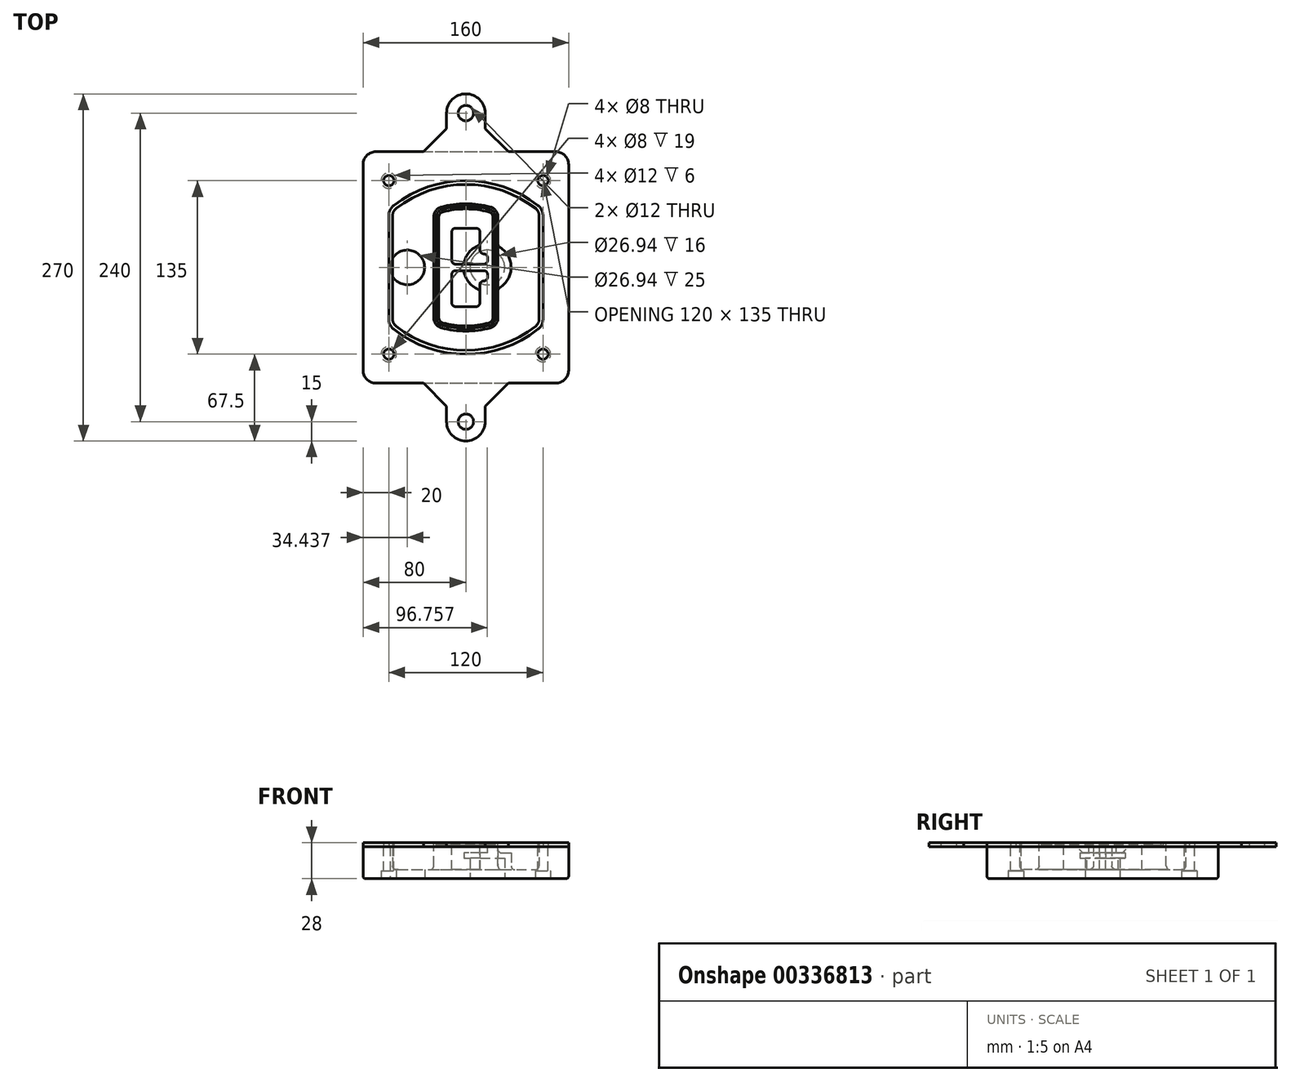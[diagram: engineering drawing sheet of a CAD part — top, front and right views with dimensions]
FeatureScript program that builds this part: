
annotation { "Feature Type Name" : "Feature", "Feature Type Description" : "" }
export const myFeature = defineFeature(function(context is Context, id is Id, definition is map)
    precondition{}
    {
        {
            var Q0;
            Q0=qCreatedBy(makeId("Top.planeOp"),FACE);
            var sketch = newSketch(context, id + "F0", { "sketchPlane" : qUnion([Q0])});
            skPoint(sketch, "E0.rect.middle", {"position": v(0, 0) * mm});
            skLineSegment(sketch, "E1.bottom", {"start": v(-70, -90) * mm, "end": v(70, -90) * mm});
            skLineSegment(sketch, "E1.top", {"start": v(-70, 90) * mm, "end": v(70, 90) * mm});
            skLineSegment(sketch, "E1.left", {"start": v(-80, -80) * mm, "end": v(-80, 80) * mm});
            skLineSegment(sketch, "E1.right", {"start": v(80, -80) * mm, "end": v(80, 80) * mm});
            skLineSegment(sketch, "E2", {"start": v(-80, 90) * mm, "end": v(80, -90) * mm, "construction": true});
            skLineSegment(sketch, "E3", {"start": v(80, 90) * mm, "end": v(-80, -90) * mm, "construction": true});
            skCircle(sketch, "E4", {"center": v(-60, 67.5) * mm, "radius": 4 * mm});
            skCircle(sketch, "E5", {"center": v(60, 67.5) * mm, "radius": 4 * mm});
            skCircle(sketch, "E6", {"center": v(60, -67.5) * mm, "radius": 4 * mm});
            skCircle(sketch, "E7", {"center": v(-60, -67.5) * mm, "radius": 4 * mm});
            skLineSegment(sketch, "E8", {"start": v(-60, 67.5) * mm, "end": v(60, 67.5) * mm, "construction": true});
            skLineSegment(sketch, "E9", {"start": v(60, 67.5) * mm, "end": v(60, -67.5) * mm, "construction": true});
            skLineSegment(sketch, "E10", {"start": v(60, -67.5) * mm, "end": v(-60, -67.5) * mm, "construction": true});
            skLineSegment(sketch, "E11", {"start": v(-60, -67.5) * mm, "end": v(-60, 67.5) * mm, "construction": true});
            skLineSegment(sketch, "E12", {"start": v(-60, 40.3) * mm, "end": v(-60, -40.3) * mm});
            skLineSegment(sketch, "E13", {"start": v(60, 40.3) * mm, "end": v(60, -40.3) * mm});
            skArc(sketch, "E14", {"start": v(56.15, 48.18) * mm, "mid": v(0, 67.5) * mm, "end": v(-56.15, 48.18) * mm});
            skArc(sketch, "E15", {"start": v(-56.15, -48.18) * mm, "mid": v(0, -67.5) * mm, "end": v(56.15, -48.18) * mm});
            skLineSegment(sketch, "E16", {"start": v(-60, 0) * mm, "end": v(60, 0) * mm, "construction": true});
            skPoint(sketch, "E17.visualSharp", {"position": v(-60, -45) * mm});
            skArc(sketch, "E17.filletArc", {"start": v(-60, -40.3) * mm, "mid": v(-58.99, -44.68) * mm, "end": v(-56.15, -48.18) * mm});
            skPoint(sketch, "E18.visualSharp", {"position": v(-60, 45) * mm});
            skArc(sketch, "E18.filletArc", {"start": v(-56.15, 48.18) * mm, "mid": v(-58.99, 44.68) * mm, "end": v(-60, 40.3) * mm});
            skPoint(sketch, "E19.visualSharp", {"position": v(60, 45) * mm});
            skArc(sketch, "E19.filletArc", {"start": v(60, 40.3) * mm, "mid": v(58.99, 44.68) * mm, "end": v(56.15, 48.18) * mm});
            skPoint(sketch, "E20.visualSharp", {"position": v(60, -45) * mm});
            skArc(sketch, "E20.filletArc", {"start": v(56.15, -48.18) * mm, "mid": v(58.99, -44.68) * mm, "end": v(60, -40.3) * mm});
            skPoint(sketch, "E21.visualSharp", {"position": v(-80, 90) * mm});
            skArc(sketch, "E21.filletArc", {"start": v(-70, 90) * mm, "mid": v(-77.07, 87.07) * mm, "end": v(-80, 80) * mm});
            skPoint(sketch, "E22.visualSharp", {"position": v(80, 90) * mm});
            skArc(sketch, "E22.filletArc", {"start": v(80, 80) * mm, "mid": v(77.07, 87.07) * mm, "end": v(70, 90) * mm});
            skPoint(sketch, "E23.visualSharp", {"position": v(80, -90) * mm});
            skArc(sketch, "E23.filletArc", {"start": v(70, -90) * mm, "mid": v(77.07, -87.07) * mm, "end": v(80, -80) * mm});
            skPoint(sketch, "E24.visualSharp", {"position": v(-80, -90) * mm});
            skArc(sketch, "E24.filletArc", {"start": v(-80, -80) * mm, "mid": v(-77.07, -87.07) * mm, "end": v(-70, -90) * mm});
            skArc(sketch, "E25.0", {"start": v(57, 40.3) * mm, "mid": v(56.3, 43.36) * mm, "end": v(54.3, 45.81) * mm});
            skLineSegment(sketch, "E25.1", {"start": v(57, 40.3) * mm, "end": v(57, -40.3) * mm});
            skArc(sketch, "E25.2", {"start": v(54.3, -45.81) * mm, "mid": v(56.3, -43.36) * mm, "end": v(57, -40.3) * mm});
            skArc(sketch, "E25.3", {"start": v(-54.3, -45.81) * mm, "mid": v(0, -64.5) * mm, "end": v(54.3, -45.81) * mm});
            skArc(sketch, "E25.4", {"start": v(-57, -40.3) * mm, "mid": v(-56.3, -43.36) * mm, "end": v(-54.3, -45.81) * mm});
            skArc(sketch, "E25.5", {"start": v(54.3, 45.81) * mm, "mid": v(0, 64.5) * mm, "end": v(-54.3, 45.81) * mm});
            skLineSegment(sketch, "E25.6", {"start": v(-57, 40.3) * mm, "end": v(-57, -40.3) * mm});
            skArc(sketch, "E25.7", {"start": v(-54.3, 45.81) * mm, "mid": v(-56.3, 43.36) * mm, "end": v(-57, 40.3) * mm});
            skArc(sketch, "E26.0", {"start": v(-58.62, 51.33) * mm, "mid": v(-62.58, 46.43) * mm, "end": v(-64, 40.3) * mm});
            skArc(sketch, "E26.1", {"start": v(58.62, 51.33) * mm, "mid": v(0, 71.5) * mm, "end": v(-58.62, 51.33) * mm});
            skArc(sketch, "E26.2", {"start": v(64, 40.3) * mm, "mid": v(62.58, 46.43) * mm, "end": v(58.62, 51.33) * mm});
            skLineSegment(sketch, "E26.3", {"start": v(64, 40.3) * mm, "end": v(64, -40.3) * mm});
            skArc(sketch, "E26.4", {"start": v(58.62, -51.33) * mm, "mid": v(62.58, -46.43) * mm, "end": v(64, -40.3) * mm});
            skLineSegment(sketch, "E26.5", {"start": v(-64, 40.3) * mm, "end": v(-64, -40.3) * mm});
            skArc(sketch, "E26.6", {"start": v(-58.62, -51.33) * mm, "mid": v(0, -71.5) * mm, "end": v(58.62, -51.33) * mm});
            skArc(sketch, "E26.7", {"start": v(-64, -40.3) * mm, "mid": v(-62.58, -46.43) * mm, "end": v(-58.62, -51.33) * mm});
            skPoint(sketch, "E27.endSnap0", {"position": v(0, 90) * mm});
            skSolve(sketch);
        }
        {
            var Q0;
            Q0=makeQuery(id+"F0.imprint","IMPRINT",FACE,{"disambiguationData":[TD([[makeQuery(id+"F0.imprint","IMPRINT",EDGE,{"derivedFrom":sQuery(id+"F0.wireOp",EDGE,"E1.bottom")}),1.0]])]});
            var Q1;
            Q1=makeQuery(id+"F0.imprint","IMPRINT",FACE,{"disambiguationData":[TD([[makeQuery(id+"F0.imprint","IMPRINT",EDGE,{"derivedFrom":sQuery(id+"F0.wireOp",EDGE,"E12")}),1.0]])]});
            var Q2;
            Q2=makeQuery(id+"F0.imprint","IMPRINT",FACE,{"disambiguationData":[TD([[makeQuery(id+"F0.imprint","IMPRINT",EDGE,{"derivedFrom":sQuery(id+"F0.wireOp",EDGE,"E25.0")}),1.0]])]});
            var Q3;
            Q3=makeQuery(id+"F0.imprint","IMPRINT",FACE,{"disambiguationData":[TD([[makeQuery(id+"F0.imprint","IMPRINT",EDGE,{"derivedFrom":sQuery(id+"F0.wireOp",EDGE,"E12")}),-1.0]])]});
            extrude(context, id + "F1", {"entities" : qUnion([Q0, Q1, Q2, Q3]), "oppositeDirection" : true, "depth" : 25 * mm});
        }
        {
            var Q0;
            Q0=makeQuery(id+"F0.imprint","IMPRINT",FACE,{"disambiguationData":[TD([[makeQuery(id+"F0.imprint","IMPRINT",EDGE,{"derivedFrom":sQuery(id+"F0.wireOp",EDGE,"E12")}),1.0]])]});
            extrude(context, id + "F2", {"entities" : qUnion([Q0]), "operationType" : NewBodyOperationType.ADD, "depth" : 3 * mm});
        }
        {
            var Q0;
            Q0=makeQuery(id+"F0.imprint","IMPRINT",FACE,{"disambiguationData":[TD([[makeQuery(id+"F0.imprint","IMPRINT",EDGE,{"derivedFrom":sQuery(id+"F0.wireOp",EDGE,"E25.0")}),1.0]])]});
            extrude(context, id + "F3", {"entities" : qUnion([Q0]), "operationType" : NewBodyOperationType.REMOVE, "oppositeDirection" : true, "depth" : 18 * mm});
        }
        {
            var Q0;
            Q0=makeQuery(id+"F2.opExtrude","CAP_FACE",FACE,{"disambiguationData":[OSD([sQuery(id+"F0.wireOp",EDGE,"E12"),sQuery(id+"F0.wireOp",EDGE,"E13"),sQuery(id+"F0.wireOp",EDGE,"E14"),sQuery(id+"F0.wireOp",EDGE,"E15"),sQuery(id+"F0.wireOp",EDGE,"E17.filletArc"),sQuery(id+"F0.wireOp",EDGE,"E18.filletArc"),sQuery(id+"F0.wireOp",EDGE,"E19.filletArc"),sQuery(id+"F0.wireOp",EDGE,"E20.filletArc"),sQuery(id+"F0.wireOp",EDGE,"E25.0"),sQuery(id+"F0.wireOp",EDGE,"E25.1"),sQuery(id+"F0.wireOp",EDGE,"E25.2"),sQuery(id+"F0.wireOp",EDGE,"E25.3"),sQuery(id+"F0.wireOp",EDGE,"E25.4"),sQuery(id+"F0.wireOp",EDGE,"E25.5"),sQuery(id+"F0.wireOp",EDGE,"E25.6"),sQuery(id+"F0.wireOp",EDGE,"E25.7")])],"isStart":false});
            var sketch = newSketch(context, id + "F4", { "sketchPlane" : qUnion([Q0])});
            skArc(sketch, "E28.0", {"start": v(-19.08, -46.97) * mm, "mid": v(0, -49.5) * mm, "end": v(19.08, -46.97) * mm});
            skArc(sketch, "E29.0", {"start": v(19.08, 46.97) * mm, "mid": v(0, 49.5) * mm, "end": v(-19.08, 46.97) * mm});
            skLineSegment(sketch, "E30", {"start": v(-25, 39.25) * mm, "end": v(-25, -39.25) * mm});
            skLineSegment(sketch, "E31", {"start": v(25, 39.25) * mm, "end": v(25, -39.25) * mm});
            skLineSegment(sketch, "E32", {"start": v(-25, 45.1) * mm, "end": v(25, 45.1) * mm, "construction": true});
            skLineSegment(sketch, "E33", {"start": v(-25, -45.1) * mm, "end": v(25, -45.1) * mm, "construction": true});
            skPoint(sketch, "E34.visualSharp", {"position": v(-25, 45.1) * mm});
            skArc(sketch, "E34.filletArc", {"start": v(-19.08, 46.97) * mm, "mid": v(-23.35, 44.11) * mm, "end": v(-25, 39.25) * mm});
            skPoint(sketch, "E35.visualSharp", {"position": v(25, 45.1) * mm});
            skArc(sketch, "E35.filletArc", {"start": v(25, 39.25) * mm, "mid": v(23.35, 44.11) * mm, "end": v(19.08, 46.97) * mm});
            skPoint(sketch, "E36.visualSharp", {"position": v(25, -45.1) * mm});
            skArc(sketch, "E36.filletArc", {"start": v(19.08, -46.97) * mm, "mid": v(23.35, -44.11) * mm, "end": v(25, -39.25) * mm});
            skPoint(sketch, "E37.visualSharp", {"position": v(-25, -45.1) * mm});
            skArc(sketch, "E37.filletArc", {"start": v(-25, -39.25) * mm, "mid": v(-23.35, -44.11) * mm, "end": v(-19.08, -46.97) * mm});
            skArc(sketch, "E38.0", {"start": v(54.3, 45.81) * mm, "mid": v(0, 64.5) * mm, "end": v(-54.3, 45.81) * mm});
            skArc(sketch, "E38.1", {"start": v(-54.3, 45.81) * mm, "mid": v(-56.3, 43.36) * mm, "end": v(-57, 40.3) * mm});
            skLineSegment(sketch, "E38.2", {"start": v(-57, 40.3) * mm, "end": v(-57, -40.3) * mm});
            skArc(sketch, "E38.3", {"start": v(-57, -40.3) * mm, "mid": v(-56.3, -43.36) * mm, "end": v(-54.3, -45.81) * mm});
            skArc(sketch, "E38.4", {"start": v(-54.3, -45.81) * mm, "mid": v(0, -64.5) * mm, "end": v(54.3, -45.81) * mm});
            skArc(sketch, "E38.5", {"start": v(54.3, -45.81) * mm, "mid": v(56.3, -43.36) * mm, "end": v(57, -40.3) * mm});
            skLineSegment(sketch, "E38.6", {"start": v(57, 40.3) * mm, "end": v(57, -40.3) * mm});
            skArc(sketch, "E38.7", {"start": v(57, 40.3) * mm, "mid": v(56.3, 43.36) * mm, "end": v(54.3, 45.81) * mm});
            skLineSegment(sketch, "E39.0", {"start": v(23, 39.25) * mm, "end": v(23, -39.25) * mm});
            skArc(sketch, "E39.1", {"start": v(18.56, -45.04) * mm, "mid": v(21.76, -42.9) * mm, "end": v(23, -39.25) * mm});
            skArc(sketch, "E39.2", {"start": v(-18.56, -45.04) * mm, "mid": v(0, -47.5) * mm, "end": v(18.56, -45.04) * mm});
            skArc(sketch, "E39.3", {"start": v(-23, -39.25) * mm, "mid": v(-21.76, -42.9) * mm, "end": v(-18.56, -45.04) * mm});
            skLineSegment(sketch, "E39.4", {"start": v(-23, 39.25) * mm, "end": v(-23, -39.25) * mm});
            skArc(sketch, "E39.5", {"start": v(23, 39.25) * mm, "mid": v(21.76, 42.9) * mm, "end": v(18.56, 45.04) * mm});
            skArc(sketch, "E39.6", {"start": v(-18.56, 45.04) * mm, "mid": v(-21.76, 42.9) * mm, "end": v(-23, 39.25) * mm});
            skArc(sketch, "E39.7", {"start": v(18.56, 45.04) * mm, "mid": v(0, 47.5) * mm, "end": v(-18.56, 45.04) * mm});
            skArc(sketch, "E40.0", {"start": v(21, 39.25) * mm, "mid": v(20.18, 41.68) * mm, "end": v(18.04, 43.1) * mm});
            skLineSegment(sketch, "E40.1", {"start": v(21, 39.25) * mm, "end": v(21, -39.25) * mm});
            skArc(sketch, "E40.2", {"start": v(18.04, -43.1) * mm, "mid": v(20.18, -41.68) * mm, "end": v(21, -39.25) * mm});
            skArc(sketch, "E40.3", {"start": v(-18.04, -43.1) * mm, "mid": v(0, -45.5) * mm, "end": v(18.04, -43.1) * mm});
            skArc(sketch, "E40.4", {"start": v(-21, -39.25) * mm, "mid": v(-20.18, -41.68) * mm, "end": v(-18.04, -43.1) * mm});
            skArc(sketch, "E40.5", {"start": v(18.04, 43.1) * mm, "mid": v(0, 45.5) * mm, "end": v(-18.04, 43.1) * mm});
            skLineSegment(sketch, "E40.6", {"start": v(-21, 39.25) * mm, "end": v(-21, -39.25) * mm});
            skArc(sketch, "E40.7", {"start": v(-18.04, 43.1) * mm, "mid": v(-20.18, 41.68) * mm, "end": v(-21, 39.25) * mm});
            skLineSegment(sketch, "E41", {"start": v(-25, 0) * mm, "end": v(25, 0) * mm, "construction": true});
            skLineSegment(sketch, "E42", {"start": v(-11, 5.5) * mm, "end": v(-11, 27.5) * mm});
            skLineSegment(sketch, "E43", {"start": v(-8, 30.5) * mm, "end": v(8, 30.5) * mm});
            skLineSegment(sketch, "E44", {"start": v(11, 27.5) * mm, "end": v(11, 13.5) * mm});
            skLineSegment(sketch, "E45", {"start": v(14, 10.5) * mm, "end": v(14, 10.5) * mm});
            skLineSegment(sketch, "E46", {"start": v(17, 7.5) * mm, "end": v(17, 5.5) * mm});
            skLineSegment(sketch, "E47", {"start": v(14, 2.5) * mm, "end": v(-8, 2.5) * mm});
            skPoint(sketch, "E48.visualSharp", {"position": v(-11, 30.5) * mm});
            skArc(sketch, "E48.filletArc", {"start": v(-8, 30.5) * mm, "mid": v(-10.12, 29.62) * mm, "end": v(-11, 27.5) * mm});
            skPoint(sketch, "E49.visualSharp", {"position": v(11, 30.5) * mm});
            skArc(sketch, "E49.filletArc", {"start": v(11, 27.5) * mm, "mid": v(10.12, 29.62) * mm, "end": v(8, 30.5) * mm});
            skPoint(sketch, "E50.visualSharp", {"position": v(11, 10.5) * mm});
            skArc(sketch, "E50.filletArc", {"start": v(11, 13.5) * mm, "mid": v(11.88, 11.38) * mm, "end": v(14, 10.5) * mm});
            skPoint(sketch, "E51.visualSharp", {"position": v(17, 10.5) * mm});
            skArc(sketch, "E51.filletArc", {"start": v(17, 7.5) * mm, "mid": v(16.12, 9.62) * mm, "end": v(14, 10.5) * mm});
            skPoint(sketch, "E52.visualSharp", {"position": v(17, 2.5) * mm});
            skArc(sketch, "E52.filletArc", {"start": v(14, 2.5) * mm, "mid": v(16.12, 3.38) * mm, "end": v(17, 5.5) * mm});
            skPoint(sketch, "E53.visualSharp", {"position": v(-11, 2.5) * mm});
            skArc(sketch, "E53.filletArc", {"start": v(-11, 5.5) * mm, "mid": v(-10.12, 3.38) * mm, "end": v(-8, 2.5) * mm});
            skLineSegment(sketch, "E54.0.MirrorCS", {"start": v(14, -2.5) * mm, "end": v(-8, -2.5) * mm});
            skArc(sketch, "E55.0.MirrorCS", {"start": v(-11, -5.5) * mm, "mid": v(-10.12, -3.38) * mm, "end": v(-8, -2.5) * mm});
            skLineSegment(sketch, "E56.0.MirrorCS", {"start": v(-11, -5.5) * mm, "end": v(-11, -27.5) * mm});
            skArc(sketch, "E57.0.MirrorCS", {"start": v(-8, -30.5) * mm, "mid": v(-10.12, -29.62) * mm, "end": v(-11, -27.5) * mm});
            skLineSegment(sketch, "E58.0.MirrorCS", {"start": v(-8, -30.5) * mm, "end": v(8, -30.5) * mm});
            skArc(sketch, "E59.0.MirrorCS", {"start": v(11, -27.5) * mm, "mid": v(10.12, -29.62) * mm, "end": v(8, -30.5) * mm});
            skLineSegment(sketch, "E60.0.MirrorCS", {"start": v(11, -27.5) * mm, "end": v(11, -13.5) * mm});
            skArc(sketch, "E61.0.MirrorCS", {"start": v(11, -13.5) * mm, "mid": v(11.88, -11.38) * mm, "end": v(14, -10.5) * mm});
            skArc(sketch, "E62.0.MirrorCS", {"start": v(17, -7.5) * mm, "mid": v(16.12, -9.62) * mm, "end": v(14, -10.5) * mm});
            skLineSegment(sketch, "E63.0.MirrorCS", {"start": v(17, -7.5) * mm, "end": v(17, -5.5) * mm});
            skArc(sketch, "E64.0.MirrorCS", {"start": v(14, -2.5) * mm, "mid": v(16.12, -3.38) * mm, "end": v(17, -5.5) * mm});
            skSolve(sketch);
        }
        {
            var Q0;
            Q0=makeQuery(id+"F4.imprint","IMPRINT",FACE,{"disambiguationData":[TD([[makeQuery(id+"F4.imprint","IMPRINT",EDGE,{"derivedFrom":sQuery(id+"F4.wireOp",EDGE,"E28.0")}),1.0]])]});
            var Q1;
            Q1=makeQuery(id+"F4.imprint","IMPRINT",FACE,{"disambiguationData":[TD([[makeQuery(id+"F4.imprint","IMPRINT",EDGE,{"derivedFrom":sQuery(id+"F4.wireOp",EDGE,"E39.0")}),-1.0]])]});
            var Q2;
            Q2=makeQuery(id+"F4.imprint","IMPRINT",FACE,{"disambiguationData":[TD([[makeQuery(id+"F4.imprint","IMPRINT",EDGE,{"derivedFrom":sQuery(id+"F4.wireOp",EDGE,"E40.0")}),1.0]])]});
            extrude(context, id + "F5", {"entities" : qUnion([Q0, Q1, Q2]), "operationType" : NewBodyOperationType.ADD, "endBound" : BoundingType.UP_TO_NEXT, "oppositeDirection" : true, "depth" : 25 * mm});
        }
        {
            var Q0;
            Q0=makeQuery(id+"F4.imprint","IMPRINT",FACE,{"disambiguationData":[TD([[makeQuery(id+"F4.imprint","IMPRINT",EDGE,{"derivedFrom":sQuery(id+"F4.wireOp",EDGE,"E39.0")}),-1.0]])]});
            extrude(context, id + "F6", {"entities" : qUnion([Q0]), "operationType" : NewBodyOperationType.REMOVE, "oppositeDirection" : true, "depth" : 2 * mm});
        }
        {
            var Q0;
            Q0=makeQuery(id+"F1.opExtrude","CAP_FACE",FACE,{"disambiguationData":[OSD([sQuery(id+"F0.wireOp",EDGE,"E1.bottom"),sQuery(id+"F0.wireOp",EDGE,"E1.top"),sQuery(id+"F0.wireOp",EDGE,"E1.left"),sQuery(id+"F0.wireOp",EDGE,"E1.right"),sQuery(id+"F0.wireOp",EDGE,"E4"),sQuery(id+"F0.wireOp",EDGE,"E5"),sQuery(id+"F0.wireOp",EDGE,"E6"),sQuery(id+"F0.wireOp",EDGE,"E7"),sQuery(id+"F0.wireOp",EDGE,"E21.filletArc"),sQuery(id+"F0.wireOp",EDGE,"E22.filletArc"),sQuery(id+"F0.wireOp",EDGE,"E23.filletArc"),sQuery(id+"F0.wireOp",EDGE,"E24.filletArc")])],"isStart":false});
            var sketch = newSketch(context, id + "F7", { "sketchPlane" : qUnion([Q0])});
            skCircle(sketch, "E65", {"center": v(16.76, 0) * mm, "radius": 13.47 * mm});
            skCircle(sketch, "E66", {"center": v(-45.56, 0) * mm, "radius": 13.47 * mm});
            skLineSegment(sketch, "E67", {"start": v(80, 0) * mm, "end": v(-80, 0) * mm});
            skCircle(sketch, "E68", {"center": v(16.76, 0) * mm, "radius": 18.47 * mm});
            skCircle(sketch, "E69", {"center": v(60, -67.5) * mm, "radius": 6 * mm});
            skCircle(sketch, "E70", {"center": v(-60, -67.5) * mm, "radius": 6 * mm});
            skCircle(sketch, "E71", {"center": v(-60, 67.5) * mm, "radius": 6 * mm});
            skCircle(sketch, "E72", {"center": v(60, 67.5) * mm, "radius": 6 * mm});
            skSolve(sketch);
        }
        {
            var Q0;
            {var subQ1=sQuery(id+"F7.wireOp",EDGE,"E67");var subQ4=sQuery(id+"F7.wireOp",EDGE,"E65");var subQ6=makeQuery(id+"F7.imprint","INTERSECT",VERTEX,{"disambiguationData":[OD(0.0)],"derivedFrom":[subQ4,subQ1]});Q0=makeQuery(id+"F7.imprint","IMPRINT",FACE,{"disambiguationData":[TD([[makeQuery(id+"F7.imprint","IMPRINT",EDGE,{"disambiguationData":[TD([[subQ6,-1.0]])],"derivedFrom":subQ4}),-1.0]])]});}
            var Q1;
            {var subQ0=sQuery(id+"F7.wireOp",EDGE,"E67");var subQ1=sQuery(id+"F7.wireOp",EDGE,"E65");var subQ3=makeQuery(id+"F7.imprint","INTERSECT",VERTEX,{"disambiguationData":[OD(0.0)],"derivedFrom":[subQ1,subQ0]});Q1=makeQuery(id+"F7.imprint","IMPRINT",FACE,{"disambiguationData":[TD([[makeQuery(id+"F7.imprint","IMPRINT",EDGE,{"disambiguationData":[TD([[subQ3,-1.0]])],"derivedFrom":subQ1}),1.0]])]});}
            var Q2;
            {var subQ0=sQuery(id+"F7.wireOp",EDGE,"E67");var subQ1=sQuery(id+"F7.wireOp",EDGE,"E65");var subQ3=makeQuery(id+"F7.imprint","INTERSECT",VERTEX,{"disambiguationData":[OD(0.0)],"derivedFrom":[subQ1,subQ0]});Q2=makeQuery(id+"F7.imprint","IMPRINT",FACE,{"disambiguationData":[TD([[makeQuery(id+"F7.imprint","IMPRINT",EDGE,{"disambiguationData":[TD([[subQ3,1.0]])],"derivedFrom":subQ1}),1.0]])]});}
            var Q3;
            {var subQ1=sQuery(id+"F7.wireOp",EDGE,"E67");var subQ4=sQuery(id+"F7.wireOp",EDGE,"E65");var subQ6=makeQuery(id+"F7.imprint","INTERSECT",VERTEX,{"disambiguationData":[OD(0.0)],"derivedFrom":[subQ4,subQ1]});Q3=makeQuery(id+"F7.imprint","IMPRINT",FACE,{"disambiguationData":[TD([[makeQuery(id+"F7.imprint","IMPRINT",EDGE,{"disambiguationData":[TD([[subQ6,1.0]])],"derivedFrom":subQ4}),-1.0]])]});}
            extrude(context, id + "F8", {"entities" : qUnion([Q0, Q1, Q2, Q3]), "operationType" : NewBodyOperationType.ADD, "oppositeDirection" : true, "depth" : 20 * mm});
        }
        {
            var Q0;
            {var subQ0=sQuery(id+"F7.wireOp",EDGE,"E67");var subQ1=sQuery(id+"F7.wireOp",EDGE,"E65");var subQ3=makeQuery(id+"F7.imprint","INTERSECT",VERTEX,{"disambiguationData":[OD(0.0)],"derivedFrom":[subQ1,subQ0]});Q0=makeQuery(id+"F7.imprint","IMPRINT",FACE,{"disambiguationData":[TD([[makeQuery(id+"F7.imprint","IMPRINT",EDGE,{"disambiguationData":[TD([[subQ3,-1.0]])],"derivedFrom":subQ1}),1.0]])]});}
            var Q1;
            {var subQ0=sQuery(id+"F7.wireOp",EDGE,"E67");var subQ1=sQuery(id+"F7.wireOp",EDGE,"E65");var subQ3=makeQuery(id+"F7.imprint","INTERSECT",VERTEX,{"disambiguationData":[OD(0.0)],"derivedFrom":[subQ1,subQ0]});Q1=makeQuery(id+"F7.imprint","IMPRINT",FACE,{"disambiguationData":[TD([[makeQuery(id+"F7.imprint","IMPRINT",EDGE,{"disambiguationData":[TD([[subQ3,1.0]])],"derivedFrom":subQ1}),1.0]])]});}
            extrude(context, id + "F9", {"entities" : qUnion([Q0, Q1]), "operationType" : NewBodyOperationType.REMOVE, "oppositeDirection" : true, "depth" : 16 * mm});
        }
        {
            var Q0;
            {var subQ0=sQuery(id+"F7.wireOp",EDGE,"E67");var subQ1=sQuery(id+"F7.wireOp",EDGE,"E66");var subQ3=makeQuery(id+"F7.imprint","INTERSECT",VERTEX,{"disambiguationData":[OD(0.0)],"derivedFrom":[subQ1,subQ0]});Q0=makeQuery(id+"F7.imprint","IMPRINT",FACE,{"disambiguationData":[TD([[makeQuery(id+"F7.imprint","IMPRINT",EDGE,{"disambiguationData":[TD([[subQ3,-1.0]])],"derivedFrom":subQ1}),1.0]])]});}
            var Q1;
            {var subQ0=sQuery(id+"F7.wireOp",EDGE,"E67");var subQ1=sQuery(id+"F7.wireOp",EDGE,"E66");var subQ3=makeQuery(id+"F7.imprint","INTERSECT",VERTEX,{"disambiguationData":[OD(0.0)],"derivedFrom":[subQ1,subQ0]});Q1=makeQuery(id+"F7.imprint","IMPRINT",FACE,{"disambiguationData":[TD([[makeQuery(id+"F7.imprint","IMPRINT",EDGE,{"disambiguationData":[TD([[subQ3,1.0]])],"derivedFrom":subQ1}),1.0]])]});}
            extrude(context, id + "F10", {"entities" : qUnion([Q0, Q1]), "operationType" : NewBodyOperationType.REMOVE, "oppositeDirection" : true, "depth" : 25 * mm});
        }
        {
            var Q0;
            Q0=makeQuery(id+"F7.imprint","IMPRINT",FACE,{"disambiguationData":[TD([[makeQuery(id+"F7.imprint","IMPRINT",EDGE,{"derivedFrom":sQuery(id+"F7.wireOp",EDGE,"E69")}),1.0]])]});
            var Q1;
            Q1=makeQuery(id+"F7.imprint","IMPRINT",FACE,{"disambiguationData":[TD([[makeQuery(id+"F7.imprint","IMPRINT",EDGE,{"derivedFrom":makeQuery(id+"F1.opExtrude","CAP_EDGE",EDGE,{"disambiguationData":[OSD([sQuery(id+"F0.wireOp",EDGE,"E5")])],"isStart":false})}),-1.0]])]});
            var Q2;
            Q2=makeQuery(id+"F7.imprint","IMPRINT",FACE,{"disambiguationData":[TD([[makeQuery(id+"F7.imprint","IMPRINT",EDGE,{"derivedFrom":sQuery(id+"F7.wireOp",EDGE,"E70")}),1.0]])]});
            var Q3;
            Q3=makeQuery(id+"F7.imprint","IMPRINT",FACE,{"disambiguationData":[TD([[makeQuery(id+"F7.imprint","IMPRINT",EDGE,{"derivedFrom":makeQuery(id+"F1.opExtrude","CAP_EDGE",EDGE,{"disambiguationData":[OSD([sQuery(id+"F0.wireOp",EDGE,"E4")])],"isStart":false})}),-1.0]])]});
            var Q4;
            Q4=makeQuery(id+"F7.imprint","IMPRINT",FACE,{"disambiguationData":[TD([[makeQuery(id+"F7.imprint","IMPRINT",EDGE,{"derivedFrom":sQuery(id+"F7.wireOp",EDGE,"E71")}),1.0]])]});
            var Q5;
            Q5=makeQuery(id+"F7.imprint","IMPRINT",FACE,{"disambiguationData":[TD([[makeQuery(id+"F7.imprint","IMPRINT",EDGE,{"derivedFrom":makeQuery(id+"F1.opExtrude","CAP_EDGE",EDGE,{"disambiguationData":[OSD([sQuery(id+"F0.wireOp",EDGE,"E7")])],"isStart":false})}),-1.0]])]});
            var Q6;
            Q6=makeQuery(id+"F7.imprint","IMPRINT",FACE,{"disambiguationData":[TD([[makeQuery(id+"F7.imprint","IMPRINT",EDGE,{"derivedFrom":sQuery(id+"F7.wireOp",EDGE,"E72")}),1.0]])]});
            var Q7;
            Q7=makeQuery(id+"F7.imprint","IMPRINT",FACE,{"disambiguationData":[TD([[makeQuery(id+"F7.imprint","IMPRINT",EDGE,{"derivedFrom":makeQuery(id+"F1.opExtrude","CAP_EDGE",EDGE,{"disambiguationData":[OSD([sQuery(id+"F0.wireOp",EDGE,"E6")])],"isStart":false})}),-1.0]])]});
            extrude(context, id + "F11", {"entities" : qUnion([Q0, Q1, Q2, Q3, Q4, Q5, Q6, Q7]), "operationType" : NewBodyOperationType.REMOVE, "oppositeDirection" : true, "depth" : 6 * mm});
        }
        {
            var Q0;
            Q0=makeQuery(id+"F9.boolean.opBoolean","COPY",FACE,{"derivedFrom":makeQuery(id+"F9.opExtrude","CAP_FACE",FACE,{"disambiguationData":[OSD([sQuery(id+"F7.wireOp",EDGE,"E65")])],"isStart":false})});
            var sketch = newSketch(context, id + "F12", { "sketchPlane" : qUnion([Q0])});
            skArc(sketch, "E73.0", {"start": v(11, 17.55) * mm, "mid": v(2.57, 11.82) * mm, "end": v(-1.54, 2.5) * mm});
            skArc(sketch, "E73.1", {"start": v(-1.54, -2.5) * mm, "mid": v(2.57, -11.82) * mm, "end": v(11, -17.55) * mm});
            skLineSegment(sketch, "E74", {"start": v(-1.54, -2.5) * mm, "end": v(14, -2.5) * mm});
            skLineSegment(sketch, "E75.0", {"start": v(14, 2.5) * mm, "end": v(-1.54, 2.5) * mm});
            skArc(sketch, "E75.1", {"start": v(14, 2.5) * mm, "mid": v(16.12, 3.38) * mm, "end": v(17, 5.5) * mm});
            skLineSegment(sketch, "E75.2", {"start": v(17, 7.5) * mm, "end": v(17, 5.5) * mm});
            skArc(sketch, "E75.3", {"start": v(17, 7.5) * mm, "mid": v(16.12, 9.62) * mm, "end": v(14, 10.5) * mm});
            skArc(sketch, "E75.4", {"start": v(11, 13.5) * mm, "mid": v(11.88, 11.38) * mm, "end": v(14, 10.5) * mm});
            skLineSegment(sketch, "E75.5", {"start": v(11, 17.55) * mm, "end": v(11, 13.5) * mm});
            skLineSegment(sketch, "E75.7", {"start": v(14, -2.5) * mm, "end": v(-1.54, -2.5) * mm});
            skArc(sketch, "E75.8", {"start": v(14, -2.5) * mm, "mid": v(16.12, -3.38) * mm, "end": v(17, -5.5) * mm});
            skLineSegment(sketch, "E75.9", {"start": v(17, -7.5) * mm, "end": v(17, -5.5) * mm});
            skArc(sketch, "E75.10", {"start": v(17, -7.5) * mm, "mid": v(16.12, -9.62) * mm, "end": v(14, -10.5) * mm});
            skArc(sketch, "E75.11", {"start": v(11, -13.5) * mm, "mid": v(11.88, -11.38) * mm, "end": v(14, -10.5) * mm});
            skLineSegment(sketch, "E75.12", {"start": v(11, -17.55) * mm, "end": v(11, -13.5) * mm});
            skPoint(sketch, "E76.orphan", {"position": v(11, -27.5) * mm});
            skPoint(sketch, "E77.orphan", {"position": v(-8, -2.5) * mm});
            skPoint(sketch, "E78.orphan", {"position": v(-8, 2.5) * mm});
            skPoint(sketch, "E79.orphan", {"position": v(11, 27.5) * mm});
            skSolve(sketch);
        }
        {
            var Q0;
            {var subQ7=sQuery(id+"F12.wireOp",EDGE,"E73.0");var subQ14=sQuery(id+"F12.wireOp",EDGE,"E73.1");var subQ16=sQuery(id+"F12.wireOp",EDGE,"E75.1");var subQ18=sQuery(id+"F12.wireOp",EDGE,"E75.8");Q0=qUnion([makeQuery(id+"F12.imprint","IMPRINT",FACE,{"disambiguationData":[TD([[makeQuery(id+"F12.imprint","IMPRINT",EDGE,{"derivedFrom":subQ7}),1.0]])]}),makeQuery(id+"F12.imprint","IMPRINT",FACE,{"disambiguationData":[TD([[makeQuery(id+"F12.imprint","IMPRINT",EDGE,{"derivedFrom":subQ14}),1.0]])]}),makeQuery(id+"F12.imprint","IMPRINT",FACE,{"disambiguationData":[TD([[makeQuery(id+"F12.imprint","IMPRINT",EDGE,{"derivedFrom":subQ16}),1.0]])]}),makeQuery(id+"F12.imprint","IMPRINT",FACE,{"disambiguationData":[TD([[makeQuery(id+"F12.imprint","IMPRINT",EDGE,{"derivedFrom":subQ18}),-1.0]])]})]);}
            var Q1;
            Q1=makeQuery(id+"F5.boolean.opBoolean","SPLIT",FACE,{"disambiguationData":[TD([makeQuery(id+"F5.opExtrude","SWEPT_FACE",FACE,{"disambiguationData":[OSD([sQuery(id+"F4.wireOp",EDGE,"E42")])]})])],"derivedFrom":makeQuery(id+"F3.boolean.opBoolean","COPY",FACE,{"derivedFrom":makeQuery(id+"F3.opExtrude","CAP_FACE",FACE,{"disambiguationData":[OSD([sQuery(id+"F0.wireOp",EDGE,"E25.0"),sQuery(id+"F0.wireOp",EDGE,"E25.1"),sQuery(id+"F0.wireOp",EDGE,"E25.2"),sQuery(id+"F0.wireOp",EDGE,"E25.3"),sQuery(id+"F0.wireOp",EDGE,"E25.4"),sQuery(id+"F0.wireOp",EDGE,"E25.5"),sQuery(id+"F0.wireOp",EDGE,"E25.6"),sQuery(id+"F0.wireOp",EDGE,"E25.7")])],"isStart":false})})});
            extrude(context, id + "F13", {"entities" : qUnion([Q0]), "operationType" : NewBodyOperationType.REMOVE, "endBound" : BoundingType.UP_TO_SURFACE, "endBoundEntityFace" : qUnion([Q1]), "depth" : 25 * mm});
        }
        {
            var Q0;
            Q0=makeQuery(id+"F3.boolean.opBoolean","COPY",EDGE,{"derivedFrom":makeQuery(id+"F3.opExtrude","CAP_EDGE",EDGE,{"disambiguationData":[OSD([sQuery(id+"F0.wireOp",EDGE,"E25.6")])],"isStart":false})});
            var Q1;
            Q1=makeQuery(id+"F8.boolean.opBoolean","INTERSECT",EDGE,{"derivedFrom":[makeQuery(id+"F5.opExtrude","SWEPT_FACE",FACE,{"disambiguationData":[OSD([sQuery(id+"F4.wireOp",EDGE,"E31")])]}),makeQuery(id+"F8.opExtrude","CAP_FACE",FACE,{"disambiguationData":[OSD([sQuery(id+"F7.wireOp",EDGE,"E68")])],"isStart":false})]});
            var Q2;
            Q2=makeQuery(id+"F8.boolean.opBoolean","INTERSECT",EDGE,{"disambiguationData":[OD(1.0)],"derivedFrom":[makeQuery(id+"F5.opExtrude","SWEPT_FACE",FACE,{"disambiguationData":[OSD([sQuery(id+"F4.wireOp",EDGE,"E31")])]}),makeQuery(id+"F8.opExtrude","SWEPT_FACE",FACE,{"disambiguationData":[OSD([sQuery(id+"F7.wireOp",EDGE,"E68")])]})]});
            var Q3;
            {var subQ0=sQuery(id+"F4.wireOp",EDGE,"E31");Q3=makeQuery(id+"F8.boolean.opBoolean","SPLIT",EDGE,{"disambiguationData":[TD([makeQuery(id+"F5.opExtrude","SWEPT_FACE",FACE,{"disambiguationData":[OSD([sQuery(id+"F4.wireOp",EDGE,"E36.filletArc")])]})])],"derivedFrom":makeQuery(id+"F5.opExtrude","CAP_EDGE",EDGE,{"disambiguationData":[OSD([subQ0])],"isStart":false})});}
            var Q4;
            {var subQ0=sQuery(id+"F0.wireOp",EDGE,"E25.7");var subQ1=sQuery(id+"F0.wireOp",EDGE,"E25.1");var subQ2=sQuery(id+"F0.wireOp",EDGE,"E25.6");var subQ3=sQuery(id+"F0.wireOp",EDGE,"E25.5");var subQ4=sQuery(id+"F0.wireOp",EDGE,"E25.4");var subQ5=sQuery(id+"F0.wireOp",EDGE,"E25.0");var subQ6=sQuery(id+"F0.wireOp",EDGE,"E25.2");var subQ7=sQuery(id+"F0.wireOp",EDGE,"E25.3");Q4=makeQuery(id+"F8.boolean.opBoolean","INTERSECT",EDGE,{"derivedFrom":[makeQuery(id+"F5.boolean.opBoolean","SPLIT",FACE,{"disambiguationData":[TD([makeQuery(id+"F2.opExtrude","SWEPT_FACE",FACE,{"disambiguationData":[OSD([subQ5])]})])],"derivedFrom":makeQuery(id+"F3.boolean.opBoolean","COPY",FACE,{"derivedFrom":makeQuery(id+"F3.opExtrude","CAP_FACE",FACE,{"disambiguationData":[OSD([subQ5,subQ1,subQ6,subQ7,subQ4,subQ3,subQ2,subQ0])],"isStart":false})})}),makeQuery(id+"F8.opExtrude","SWEPT_FACE",FACE,{"disambiguationData":[OSD([sQuery(id+"F7.wireOp",EDGE,"E68")])]})]});}
            var Q5;
            Q5=makeQuery(id+"F8.boolean.opBoolean","INTERSECT",EDGE,{"disambiguationData":[OD(0.0)],"derivedFrom":[makeQuery(id+"F5.opExtrude","SWEPT_FACE",FACE,{"disambiguationData":[OSD([sQuery(id+"F4.wireOp",EDGE,"E31")])]}),makeQuery(id+"F8.opExtrude","SWEPT_FACE",FACE,{"disambiguationData":[OSD([sQuery(id+"F7.wireOp",EDGE,"E68")])]})]});
            fillet(context, id + "F14", {"entities" : qUnion([Q0, Q1, Q2, Q3, Q4, Q5]), "radius" : 3 * mm, "tangentPropagation" : true, "allowEdgeOverflow" : false});
        }
        {
            var Q0;
            Q0=makeQuery(id+"F1.opExtrude","CAP_EDGE",EDGE,{"disambiguationData":[OSD([sQuery(id+"F0.wireOp",EDGE,"E1.bottom")])],"isStart":false});
            fillet(context, id + "F15", {"entities" : qUnion([Q0]), "radius" : 2 * mm, "tangentPropagation" : true, "allowEdgeOverflow" : false});
        }
        {
            var Q0;
            {var subQ0=sQuery(id+"F0.wireOp",EDGE,"E21.filletArc");var subQ1=sQuery(id+"F0.wireOp",EDGE,"E7");var subQ2=sQuery(id+"F0.wireOp",EDGE,"E6");var subQ3=sQuery(id+"F0.wireOp",EDGE,"E5");var subQ4=sQuery(id+"F0.wireOp",EDGE,"E4");var subQ5=sQuery(id+"F0.wireOp",EDGE,"E22.filletArc");var subQ6=sQuery(id+"F0.wireOp",EDGE,"E1.bottom");var subQ7=sQuery(id+"F0.wireOp",EDGE,"E1.right");var subQ8=sQuery(id+"F0.wireOp",EDGE,"E1.top");var subQ9=sQuery(id+"F0.wireOp",EDGE,"E1.left");var subQ10=sQuery(id+"F0.wireOp",EDGE,"E23.filletArc");var subQ11=sQuery(id+"F0.wireOp",EDGE,"E24.filletArc");Q0=makeQuery(id+"F2.boolean.opBoolean","SPLIT",FACE,{"disambiguationData":[TD([makeQuery(id+"F1.opExtrude","SWEPT_FACE",FACE,{"disambiguationData":[OSD([subQ6])]})])],"derivedFrom":makeQuery(id+"F1.opExtrude","CAP_FACE",FACE,{"disambiguationData":[OSD([subQ6,subQ8,subQ9,subQ7,subQ4,subQ3,subQ2,subQ1,subQ0,subQ5,subQ10,subQ11])],"isStart":true})});}
            var sketch = newSketch(context, id + "F16", { "sketchPlane" : qUnion([Q0])});
            skLineSegment(sketch, "E80.0", {"start": v(-80, -80) * mm, "end": v(-80, 80) * mm});
            skArc(sketch, "E81.0", {"start": v(-70, 90) * mm, "mid": v(-77.07, 87.07) * mm, "end": v(-80, 80) * mm});
            skLineSegment(sketch, "E82.0", {"start": v(-70, 90) * mm, "end": v(70, 90) * mm});
            skArc(sketch, "E83.0", {"start": v(80, 80) * mm, "mid": v(77.07, 87.07) * mm, "end": v(70, 90) * mm});
            skArc(sketch, "E84.0", {"start": v(-80, -80) * mm, "mid": v(-77.07, -87.07) * mm, "end": v(-70, -90) * mm});
            skLineSegment(sketch, "E85.0", {"start": v(-70, -90) * mm, "end": v(70, -90) * mm});
            skCircle(sketch, "E86.0", {"center": v(60, -67.5) * mm, "radius": 4 * mm});
            skLineSegment(sketch, "E87.0", {"start": v(80, -80) * mm, "end": v(80, 80) * mm});
            skArc(sketch, "E88.0", {"start": v(70, -90) * mm, "mid": v(77.07, -87.07) * mm, "end": v(80, -80) * mm});
            skCircle(sketch, "E89.0", {"center": v(60, 67.5) * mm, "radius": 4 * mm});
            skCircle(sketch, "E90.0", {"center": v(-60, 67.5) * mm, "radius": 4 * mm});
            skCircle(sketch, "E91.0", {"center": v(-60, -67.5) * mm, "radius": 4 * mm});
            skLineSegment(sketch, "E92.0", {"start": v(-60, 40.3) * mm, "end": v(-60, -40.3) * mm});
            skArc(sketch, "E93.0", {"start": v(56.15, 48.18) * mm, "mid": v(0, 67.5) * mm, "end": v(-56.15, 48.18) * mm});
            skArc(sketch, "E94.0", {"start": v(-56.15, -48.18) * mm, "mid": v(0, -67.5) * mm, "end": v(56.15, -48.18) * mm});
            skLineSegment(sketch, "E95.0", {"start": v(60, 40.3) * mm, "end": v(60, -40.3) * mm});
            skArc(sketch, "E96.0", {"start": v(-60, -40.3) * mm, "mid": v(-58.99, -44.68) * mm, "end": v(-56.15, -48.18) * mm});
            skArc(sketch, "E97.0", {"start": v(-56.15, 48.18) * mm, "mid": v(-58.99, 44.68) * mm, "end": v(-60, 40.3) * mm});
            skArc(sketch, "E98.0", {"start": v(60, 40.3) * mm, "mid": v(58.99, 44.68) * mm, "end": v(56.15, 48.18) * mm});
            skArc(sketch, "E99.0", {"start": v(56.15, -48.18) * mm, "mid": v(58.99, -44.68) * mm, "end": v(60, -40.3) * mm});
            skLineSegment(sketch, "E100", {"start": v(0, 90) * mm, "end": v(0, 120) * mm, "construction": true});
            skCircle(sketch, "E101", {"center": v(0, 120) * mm, "radius": 6 * mm});
            skArc(sketch, "E102", {"start": v(15, 120) * mm, "mid": v(0, 135) * mm, "end": v(-15, 120) * mm});
            skLineSegment(sketch, "E103", {"start": v(-15, 120) * mm, "end": v(-15, 108) * mm});
            skLineSegment(sketch, "E104", {"start": v(15, 120) * mm, "end": v(15, 108) * mm});
            skLineSegment(sketch, "E105", {"start": v(-15, 108) * mm, "end": v(-33, 90) * mm});
            skLineSegment(sketch, "E106", {"start": v(15, 108) * mm, "end": v(33, 90) * mm});
            skArc(sketch, "E107.MirrorCS", {"start": v(-15, 120) * mm, "mid": v(0, 135) * mm, "end": v(15, 120) * mm});
            skArc(sketch, "E108.MirrorCS", {"start": v(-60, 40.3) * mm, "mid": v(-58.99, 44.68) * mm, "end": v(-56.15, 48.18) * mm});
            skArc(sketch, "E109.MirrorCS", {"start": v(-80, 80) * mm, "mid": v(-77.07, 87.07) * mm, "end": v(-70, 90) * mm});
            skArc(sketch, "E110.MirrorCS", {"start": v(-56.15, -48.18) * mm, "mid": v(-58.99, -44.68) * mm, "end": v(-60, -40.3) * mm});
            skLineSegment(sketch, "E111.MirrorCS", {"start": v(70, -90) * mm, "end": v(-70, -90) * mm});
            skLineSegment(sketch, "E112", {"start": v(-80, 0) * mm, "end": v(80, 0) * mm, "construction": true});
            skLineSegment(sketch, "E113.MirrorCS", {"start": v(-15, -120) * mm, "end": v(-15, -108) * mm});
            skArc(sketch, "E114.MirrorCS", {"start": v(-15, -120) * mm, "mid": v(0, -135) * mm, "end": v(15, -120) * mm});
            skCircle(sketch, "E115.MirrorC", {"center": v(0, -120) * mm, "radius": 6 * mm});
            skLineSegment(sketch, "E116.MirrorCS", {"start": v(15, -120) * mm, "end": v(15, -108) * mm});
            skLineSegment(sketch, "E117.MirrorCS", {"start": v(15, -108) * mm, "end": v(33, -90) * mm});
            skLineSegment(sketch, "E118.MirrorCS", {"start": v(-15, -108) * mm, "end": v(-33, -90) * mm});
            skLineSegment(sketch, "E119.MirrorCS", {"start": v(0, -90) * mm, "end": v(0, -120) * mm, "construction": true});
            skSolve(sketch);
        }
        {
            var Q0;
            Q0 = qSketchRegion(id + "F16", true);
            var Q1;
            Q1=makeQuery(id+"F2.opExtrude","CAP_FACE",FACE,{"disambiguationData":[OSD([sQuery(id+"F0.wireOp",EDGE,"E12"),sQuery(id+"F0.wireOp",EDGE,"E13"),sQuery(id+"F0.wireOp",EDGE,"E14"),sQuery(id+"F0.wireOp",EDGE,"E15"),sQuery(id+"F0.wireOp",EDGE,"E17.filletArc"),sQuery(id+"F0.wireOp",EDGE,"E18.filletArc"),sQuery(id+"F0.wireOp",EDGE,"E19.filletArc"),sQuery(id+"F0.wireOp",EDGE,"E20.filletArc"),sQuery(id+"F0.wireOp",EDGE,"E25.0"),sQuery(id+"F0.wireOp",EDGE,"E25.1"),sQuery(id+"F0.wireOp",EDGE,"E25.2"),sQuery(id+"F0.wireOp",EDGE,"E25.3"),sQuery(id+"F0.wireOp",EDGE,"E25.4"),sQuery(id+"F0.wireOp",EDGE,"E25.5"),sQuery(id+"F0.wireOp",EDGE,"E25.6"),sQuery(id+"F0.wireOp",EDGE,"E25.7")])],"isStart":false});
            extrude(context, id + "F17", {"entities" : qUnion([Q0]), "endBound" : BoundingType.UP_TO_SURFACE, "endBoundEntityFace" : qUnion([Q1]), "depth" : 25 * mm});
        }
    });
